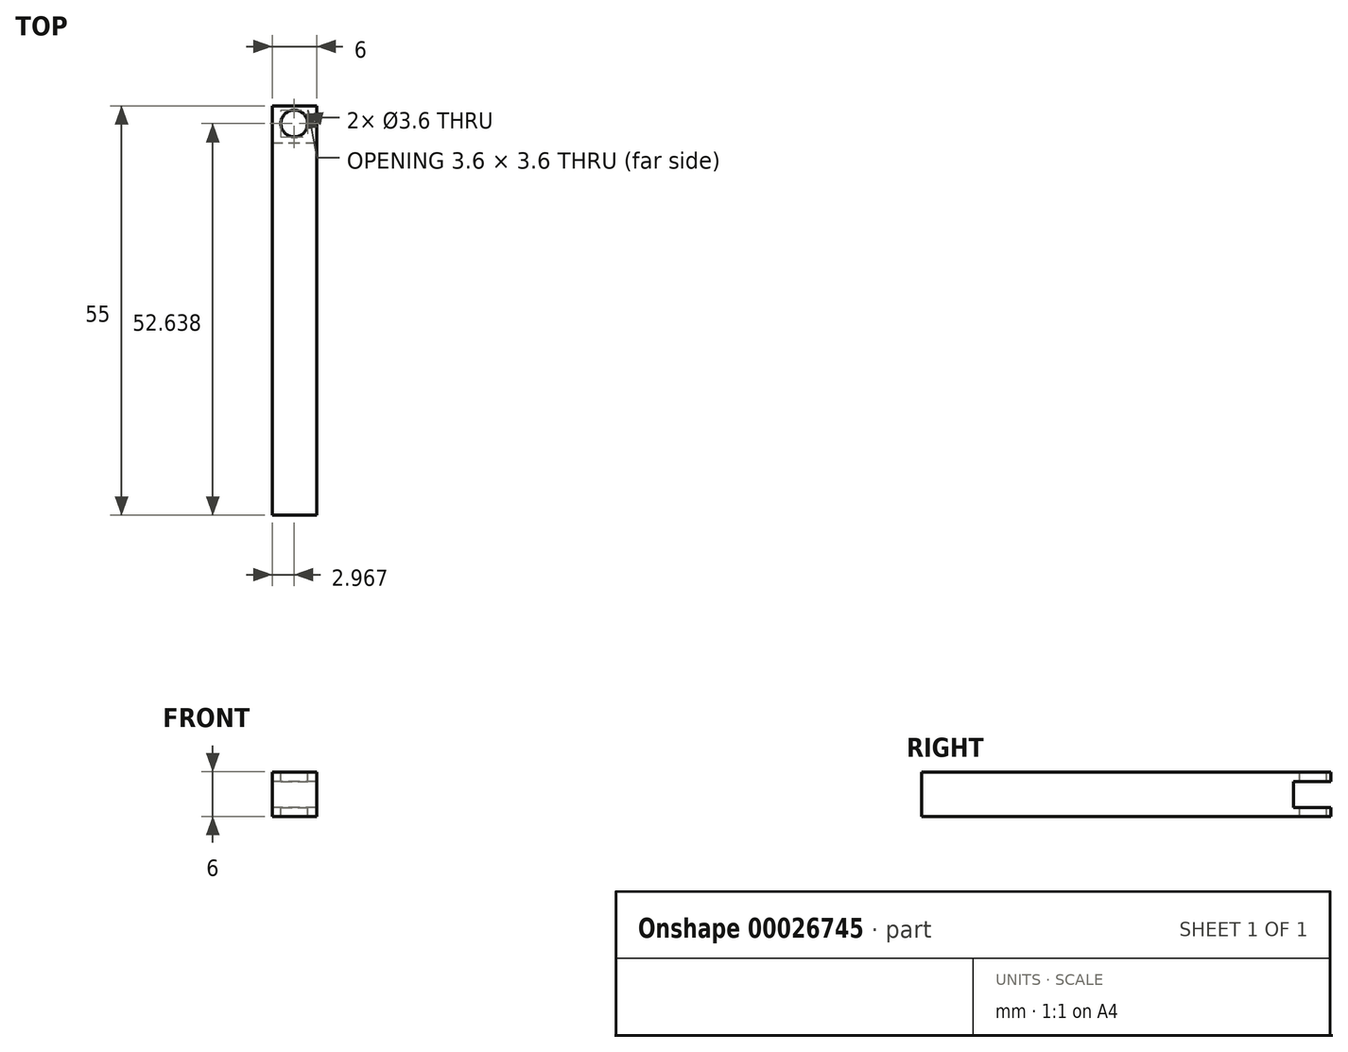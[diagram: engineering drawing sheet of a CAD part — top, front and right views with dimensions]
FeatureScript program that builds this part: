
annotation { "Feature Type Name" : "Feature", "Feature Type Description" : "" }
export const myFeature = defineFeature(function(context is Context, id is Id, definition is map)
    precondition{}
    {
        {
            var Q0;
            Q0=qCreatedBy(makeId("Front.planeOp"),FACE);
            var sketch = newSketch(context, id + "F0", { "sketchPlane" : qUnion([Q0])});
            skLineSegment(sketch, "E0.bottom", {"start": v(-13.13, 19.39) * mm, "end": v(-7.13, 19.39) * mm});
            skLineSegment(sketch, "E0.top", {"start": v(-13.13, 13.39) * mm, "end": v(-7.13, 13.39) * mm});
            skLineSegment(sketch, "E0.left", {"start": v(-13.13, 19.39) * mm, "end": v(-13.13, 13.39) * mm});
            skLineSegment(sketch, "E0.right", {"start": v(-7.13, 19.39) * mm, "end": v(-7.13, 13.39) * mm});
            skSolve(sketch);
        }
        {
            var Q0;
            Q0=makeQuery(id+"F0.imprint","IMPRINT",FACE,{"disambiguationData":[TD([[makeQuery(id+"F0.imprint","IMPRINT",EDGE,{"derivedFrom":sQuery(id+"F0.wireOp",EDGE,"E0.bottom")}),-1.0]])]});
            extrude(context, id + "F1", {"entities" : qUnion([Q0]), "depth" : 55 * mm});
        }
        {
            var Q0;
            Q0=makeQuery(id+"F1.opExtrude","SWEPT_FACE",FACE,{"disambiguationData":[OSD([sQuery(id+"F0.wireOp",EDGE,"E0.left")])]});
            var sketch = newSketch(context, id + "F2", { "sketchPlane" : qUnion([Q0])});
            skLineSegment(sketch, "E1.bottom", {"start": v(0, 18.09) * mm, "end": v(5, 18.09) * mm});
            skLineSegment(sketch, "E1.top", {"start": v(0, 14.59) * mm, "end": v(5, 14.59) * mm});
            skLineSegment(sketch, "E1.left", {"start": v(0, 18.09) * mm, "end": v(0, 14.59) * mm});
            skLineSegment(sketch, "E1.right", {"start": v(5, 18.09) * mm, "end": v(5, 14.59) * mm});
            skSolve(sketch);
        }
        {
            var Q0;
            Q0 = qSketchRegion(id + "F2", true);
            extrude(context, id + "F3", {"entities" : qUnion([Q0]), "operationType" : NewBodyOperationType.REMOVE, "endBound" : BoundingType.THROUGH_ALL, "oppositeDirection" : true, "depth" : 25 * mm});
        }
        {
            var Q0;
            Q0=makeQuery(id+"F1.opExtrude","SWEPT_FACE",FACE,{"disambiguationData":[OSD([sQuery(id+"F0.wireOp",EDGE,"E0.bottom")])]});
            var sketch = newSketch(context, id + "F4", { "sketchPlane" : qUnion([Q0])});
            skCircle(sketch, "E2", {"center": v(-10.16, -2.36) * mm, "radius": 1.8 * mm});
            skSolve(sketch);
        }
        {
            var Q0;
            Q0 = qSketchRegion(id + "F4", true);
            extrude(context, id + "F5", {"entities" : qUnion([Q0]), "operationType" : NewBodyOperationType.REMOVE, "endBound" : BoundingType.THROUGH_ALL, "oppositeDirection" : true, "depth" : 25 * mm});
        }
    });
